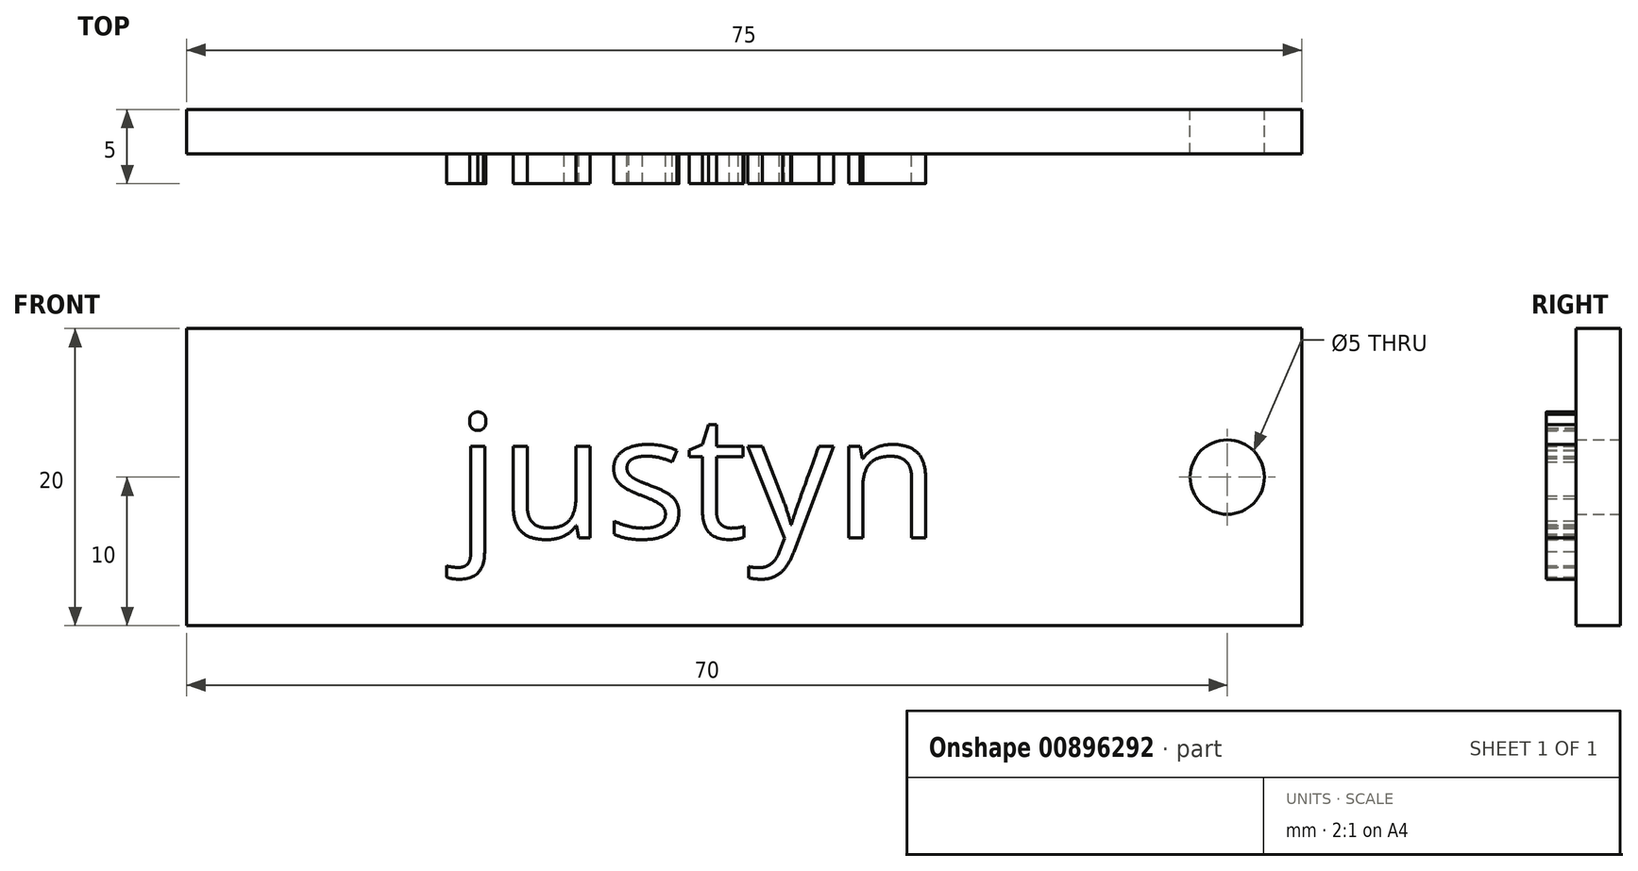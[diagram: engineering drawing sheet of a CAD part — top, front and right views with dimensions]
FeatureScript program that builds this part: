
annotation { "Feature Type Name" : "Feature", "Feature Type Description" : "" }
export const myFeature = defineFeature(function(context is Context, id is Id, definition is map)
    precondition{}
    {
        {
            var Q0;
            Q0=qCreatedBy(makeId("Front.planeOp"),FACE);
            var sketch = newSketch(context, id + "F0", { "sketchPlane" : qUnion([Q0])});
            skLineSegment(sketch, "E0.bottom", {"start": v(0, 0) * mm, "end": v(75, 0) * mm});
            skLineSegment(sketch, "E0.top", {"start": v(0, -20) * mm, "end": v(75, -20) * mm});
            skLineSegment(sketch, "E0.left", {"start": v(0, 0) * mm, "end": v(0, -20) * mm});
            skLineSegment(sketch, "E0.right", {"start": v(75, 0) * mm, "end": v(75, -20) * mm});
            skCircle(sketch, "E1", {"center": v(70, -10) * mm, "radius": 2.5 * mm});
            skSolve(sketch);
        }
        {
            var Q0;
            Q0=makeQuery(id+"F0.imprint","IMPRINT",FACE,{"disambiguationData":[TD([[makeQuery(id+"F0.imprint","IMPRINT",EDGE,{"derivedFrom":sQuery(id+"F0.wireOp",EDGE,"E0.bottom")}),-1.0]])]});
            extrude(context, id + "F1", {"entities" : qUnion([Q0]), "depth" : 3 * mm, "offsetDistance" : 25 * mm});
        }
        {
            var Q0;
            Q0=makeQuery(id+"F1.opExtrude","CAP_FACE",FACE,{"disambiguationData":[OSD([sQuery(id+"F0.wireOp",EDGE,"E0.bottom"),sQuery(id+"F0.wireOp",EDGE,"E0.top"),sQuery(id+"F0.wireOp",EDGE,"E0.left"),sQuery(id+"F0.wireOp",EDGE,"E0.right"),sQuery(id+"F0.wireOp",EDGE,"E1")])],"isStart":false});
            var sketch = newSketch(context, id + "F2", { "sketchPlane" : qUnion([Q0])});
            skText(sketch, "E2", { "text": "justyn", "fontName": "OpenSans-Regular.ttf"});
            const initialGuessF2  = {"E2": [0.01811, -0.0141, 1, 0, 0.00832]};
            skSetInitialGuess(sketch, initialGuessF2);
            skSolve(sketch);
        }
        {
            var Q0;
            Q0 = qSketchRegion(id + "F2", true);
            extrude(context, id + "F3", {"entities" : qUnion([Q0]), "operationType" : NewBodyOperationType.ADD, "depth" : 2 * mm, "offsetDistance" : 25 * mm});
        }
    });
